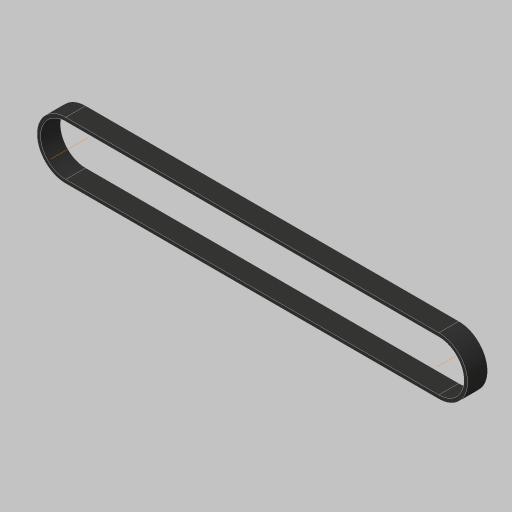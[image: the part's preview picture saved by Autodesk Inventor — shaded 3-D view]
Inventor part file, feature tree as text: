
AUTODESK INVENTOR PART (.ipt)
format: ipt  version: 2023.5 (Build 275446000, 446)  size: 159,744 bytes
history: native  units: in
note: dims shown in document units (in); Inventor stores cm internally (conversion verified against a paired STEP export)
features: sketch x3, extrude x1, other x1, projected_geometry x1
ambient origin geometry x8: Origin, YZ Plane, XZ Plane, XY Plane, X Axis, Y Axis, Z Axis, Center Point
bodies: Body1 (feature_tree)
feature tree (6):
  sketch  "Sketch2"  dims[d0=0.9023in d1=0.9023in]
  extrude  "Extrusion2"  Depth=0.9023in
  sketch  "Sketch5"  dims[d3=1.4174in d5=6.2598in d9=0.0787in d10=0.0598in d11=0.0299in d12=0.0219in d13=0.0219in d14=0.0059in d15=0.0059in d20=0.3346in d21=0.0in d22=0.0787in d23=0.0598in d24=0.0299in d25=0.0219in d26=0.0219in d27=0.0059in d28=0.0059in d29=0.0299in d30=0.0394in d31=0.0787in d32=0.0232in d34=0.0219in d35=0.0in d36=0.0in d37=0.0059in d38=0.0022in d39=0.0022in d40=0.0in d41=0.0in d42=0.0081in d43=0.0081in d44=0.0299in]
  other  "Work Axis1"
  sketch  "Sketch4"  dims[d2=1.4174in]
  projected_geometry  "Projected Loop1"
